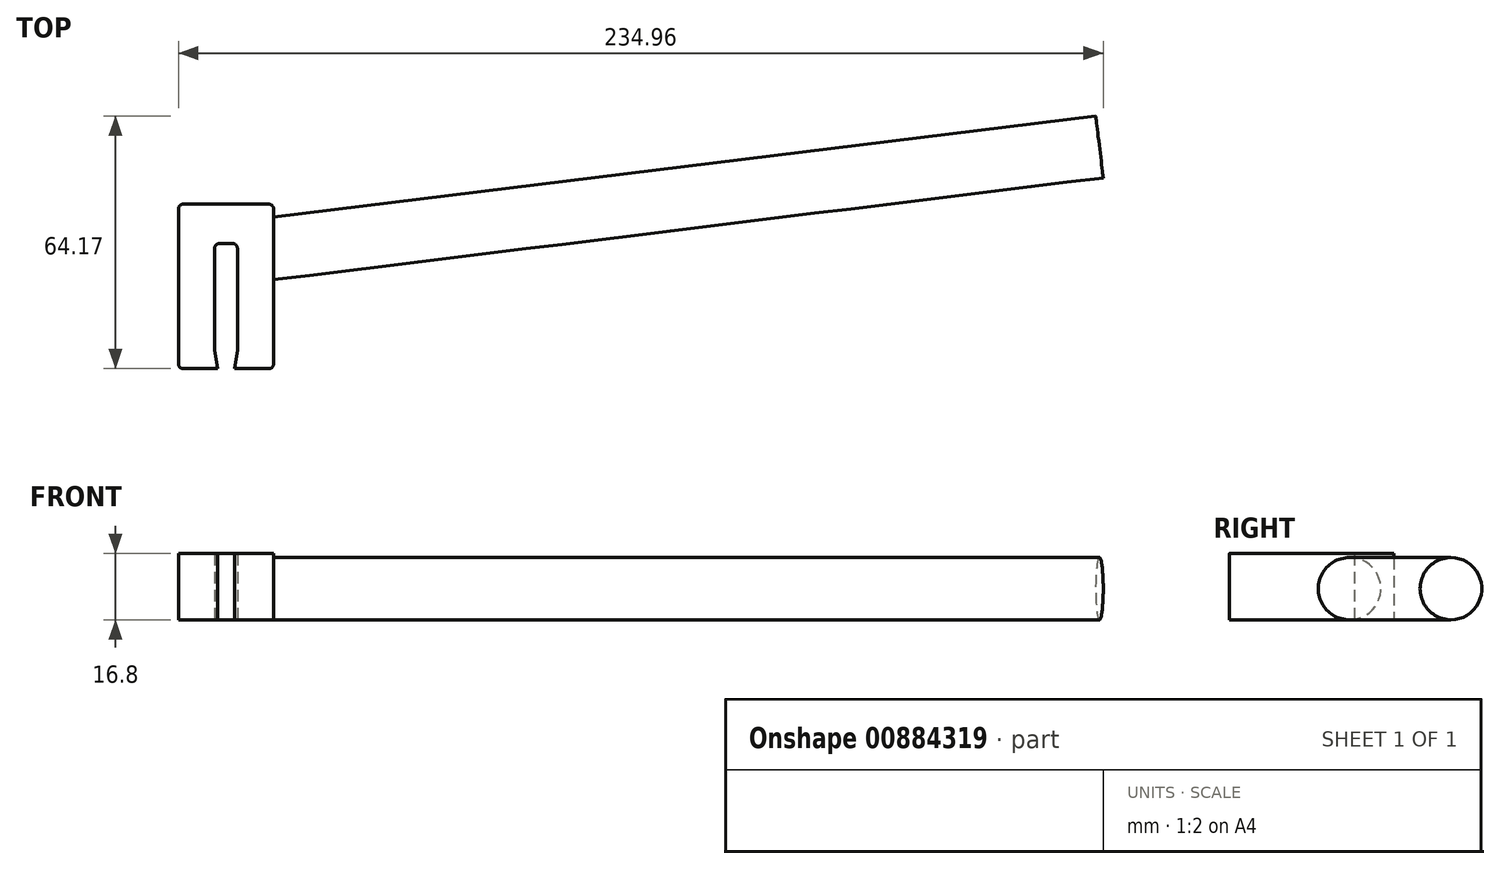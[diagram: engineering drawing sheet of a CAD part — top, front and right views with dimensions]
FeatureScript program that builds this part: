
annotation { "Feature Type Name" : "Feature", "Feature Type Description" : "" }
export const myFeature = defineFeature(function(context is Context, id is Id, definition is map)
    precondition{}
    {
        {
            var Q0;
            Q0=qCreatedBy(makeId("Top.planeOp"),FACE);
            var sketch = newSketch(context, id + "F0", { "sketchPlane" : qUnion([Q0])});
            skLineSegment(sketch, "E0.right", {"start": v(-5.8, 0) * mm, "end": v(-5.8, 27) * mm});
            skLineSegment(sketch, "E1.right", {"start": v(0, 27) * mm, "end": v(0, 0) * mm});
            skLineSegment(sketch, "E2", {"start": v(9.2, 37) * mm, "end": v(9.2, -4.79) * mm});
            skLineSegment(sketch, "E3", {"start": v(-5.1, -4.79) * mm, "end": v(-5.8, 0) * mm});
            skLineSegment(sketch, "E4", {"start": v(-0.7, -4.79) * mm, "end": v(0, 0) * mm});
            skLineSegment(sketch, "E5", {"start": v(9.2, 37) * mm, "end": v(-15, 37) * mm});
            skLineSegment(sketch, "E6", {"start": v(-15, 37) * mm, "end": v(-15, -4.79) * mm});
            skLineSegment(sketch, "E7", {"start": v(0, 27) * mm, "end": v(-5.8, 27) * mm});
            skLineSegment(sketch, "E8", {"start": v(-5.1, -4.79) * mm, "end": v(-15, -4.79) * mm});
            skLineSegment(sketch, "E9", {"start": v(9.2, -4.79) * mm, "end": v(-0.7, -4.79) * mm});
            skSolve(sketch);
        }
        {
            var Q0;
            Q0=makeQuery(id+"F0.imprint","IMPRINT",FACE,{"disambiguationData":[TD([[makeQuery(id+"F0.imprint","IMPRINT",EDGE,{"derivedFrom":sQuery(id+"F0.wireOp",EDGE,"E0.right")}),1.0]])]});
            extrude(context, id + "F1", {"entities" : qUnion([Q0]), "flatOperationType" : FlatOperationType.REMOVE, "depth" : 16.8 * mm, "offsetDistance" : 25 * mm, "domain" : OperationDomain.MODEL});
        }
        {
            var Q0;
            Q0=qCreatedBy(makeId("Right.planeOp"),FACE);
            var Q1;
            Q1=makeQuery(id+"F1.opExtrude","SWEPT_EDGE",EDGE,{"disambiguationData":[OSD([sQuery(id+"F0.wireOp",EDGE,"E2"),sQuery(id+"F0.wireOp",EDGE,"E5")])]});
            cPlane(context, id + "F2", {"entities" : qUnion([Q0, Q1]), "cplaneType" : CPlaneType.LINE_ANGLE, "offset" : 25 * mm, "angle" : 7 * degree, "oppositeDirection" : true, "width" : 150 * mm, "height" : 150 * mm});
        }
        {
            var Q0;
            Q0=makeQuery(id+"F1.opExtrude","SWEPT_EDGE",EDGE,{"disambiguationData":[OSD([sQuery(id+"F0.wireOp",EDGE,"PczdBa6P-nFhw-pfaQ-qJhu-VVp3lQY8YuxU.bottom"),sQuery(id+"F0.wireOp",EDGE,"PczdBa6P-nFhw-pfaQ-qJhu-VVp3lQY8YuxU.left")])]});
            var Q1;
            Q1=makeQuery(id+"F1.opExtrude","SWEPT_EDGE",EDGE,{"disambiguationData":[OSD([sQuery(id+"F0.wireOp",EDGE,"PczdBa6P-nFhw-pfaQ-qJhu-VVp3lQY8YuxU.bottom"),sQuery(id+"F0.wireOp",EDGE,"E2")])]});
            var Q2;
            Q2=makeQuery(id+"F1.opExtrude","SWEPT_EDGE",EDGE,{"disambiguationData":[OSD([sQuery(id+"F0.wireOp",EDGE,"E2"),sQuery(id+"F0.wireOp",EDGE,"aoy2P97I-7hsh-VHDM-M3ku-ahT5R2Tx9LTX")])]});
            var Q3;
            Q3=makeQuery(id+"F1.opExtrude","SWEPT_EDGE",EDGE,{"disambiguationData":[OSD([sQuery(id+"F0.wireOp",EDGE,"PczdBa6P-nFhw-pfaQ-qJhu-VVp3lQY8YuxU.top"),sQuery(id+"F0.wireOp",EDGE,"PczdBa6P-nFhw-pfaQ-qJhu-VVp3lQY8YuxU.left")])]});
            var Q4;
            Q4=makeQuery(id+"F1.opExtrude","SWEPT_EDGE",EDGE,{"disambiguationData":[OSD([sQuery(id+"F0.wireOp",EDGE,"E5"),sQuery(id+"F0.wireOp",EDGE,"E6")])]});
            var Q5;
            Q5=makeQuery(id+"F1.opExtrude","SWEPT_EDGE",EDGE,{"disambiguationData":[OSD([sQuery(id+"F0.wireOp",EDGE,"Kk7slsz5-66Gi-j0UX-8zI3-G2yXRSJplegM"),sQuery(id+"F0.wireOp",EDGE,"E6")])]});
            var Q6;
            Q6=makeQuery(id+"F1.opExtrude","SWEPT_EDGE",EDGE,{"disambiguationData":[OSD([sQuery(id+"F0.wireOp",EDGE,"E0.right"),sQuery(id+"F0.wireOp",EDGE,"E3")])]});
            var Q7;
            Q7=makeQuery(id+"F1.opExtrude","SWEPT_EDGE",EDGE,{"disambiguationData":[OSD([sQuery(id+"F0.wireOp",EDGE,"E1.right"),sQuery(id+"F0.wireOp",EDGE,"E4")])]});
            var Q8;
            Q8=makeQuery(id+"F1.opExtrude","SWEPT_EDGE",EDGE,{"disambiguationData":[OSD([sQuery(id+"F0.wireOp",EDGE,"E0.right"),sQuery(id+"F0.wireOp",EDGE,"E7")])]});
            var Q9;
            Q9=makeQuery(id+"F1.opExtrude","SWEPT_EDGE",EDGE,{"disambiguationData":[OSD([sQuery(id+"F0.wireOp",EDGE,"E1.right"),sQuery(id+"F0.wireOp",EDGE,"E7")])]});
            fillet(context, id + "F3", {"entities" : qUnion([Q0, Q1, Q2, Q3, Q4, Q5, Q6, Q7, Q8, Q9]), "radius" : 1.25 * mm, "tangentPropagation" : true, "defaultsChanged" : true, "vertexSettings" : [], "allowEdgeOverflow" : false});
        }
        {
            var Q0;
            Q0=qCreatedBy(id+"F2.planeOp",FACE);
            var sketch = newSketch(context, id + "F4", { "sketchPlane" : qUnion([Q0])});
            skCircle(sketch, "E10", {"center": v(-24.46, 7.9) * mm, "radius": 7.9 * mm});
            skSolve(sketch);
        }
        {
            var Q0;
            Q0=makeQuery(id+"F4.imprint","IMPRINT",FACE,{"disambiguationData":[TD([[makeQuery(id+"F4.imprint","IMPRINT",EDGE,{"derivedFrom":sQuery(id+"F4.wireOp",EDGE,"E10")}),1.0]])]});
            extrude(context, id + "F5", {"entities" : qUnion([Q0]), "operationType" : NewBodyOperationType.ADD, "flatOperationType" : FlatOperationType.REMOVE, "oppositeDirection" : true, "depth" : 210 * mm, "offsetDistance" : 25 * mm, "hasSecondDirection" : true, "secondDirectionOppositeDirection" : true, "secondDirectionDepth" : -6 * mm, "domain" : OperationDomain.MODEL});
        }
        {
            var Q0;
            Q0=makeQuery(id+"F1.opExtrude","SWEPT_FACE",FACE,{"disambiguationData":[OSD([sQuery(id+"F0.wireOp",EDGE,"E2")])]});
            var sketch = newSketch(context, id + "F6", { "sketchPlane" : qUnion([Q0])});
            skSolve(sketch);
        }
        {
            var Q0;
            Q0=qCreatedBy(id+"F2.planeOp",FACE);
            var Q1;
            Q1 = qBodyType(qCreatedBy(id + "F6" ,EDGE), BodyType.WIRE);
            cPlane(context, id + "F7", {"entities" : qUnion([Q0, Q1]), "cplaneType" : CPlaneType.OFFSET, "offset" : 10 * mm, "oppositeDirection" : true, "width" : 150 * mm, "height" : 150 * mm});
        }
    });
